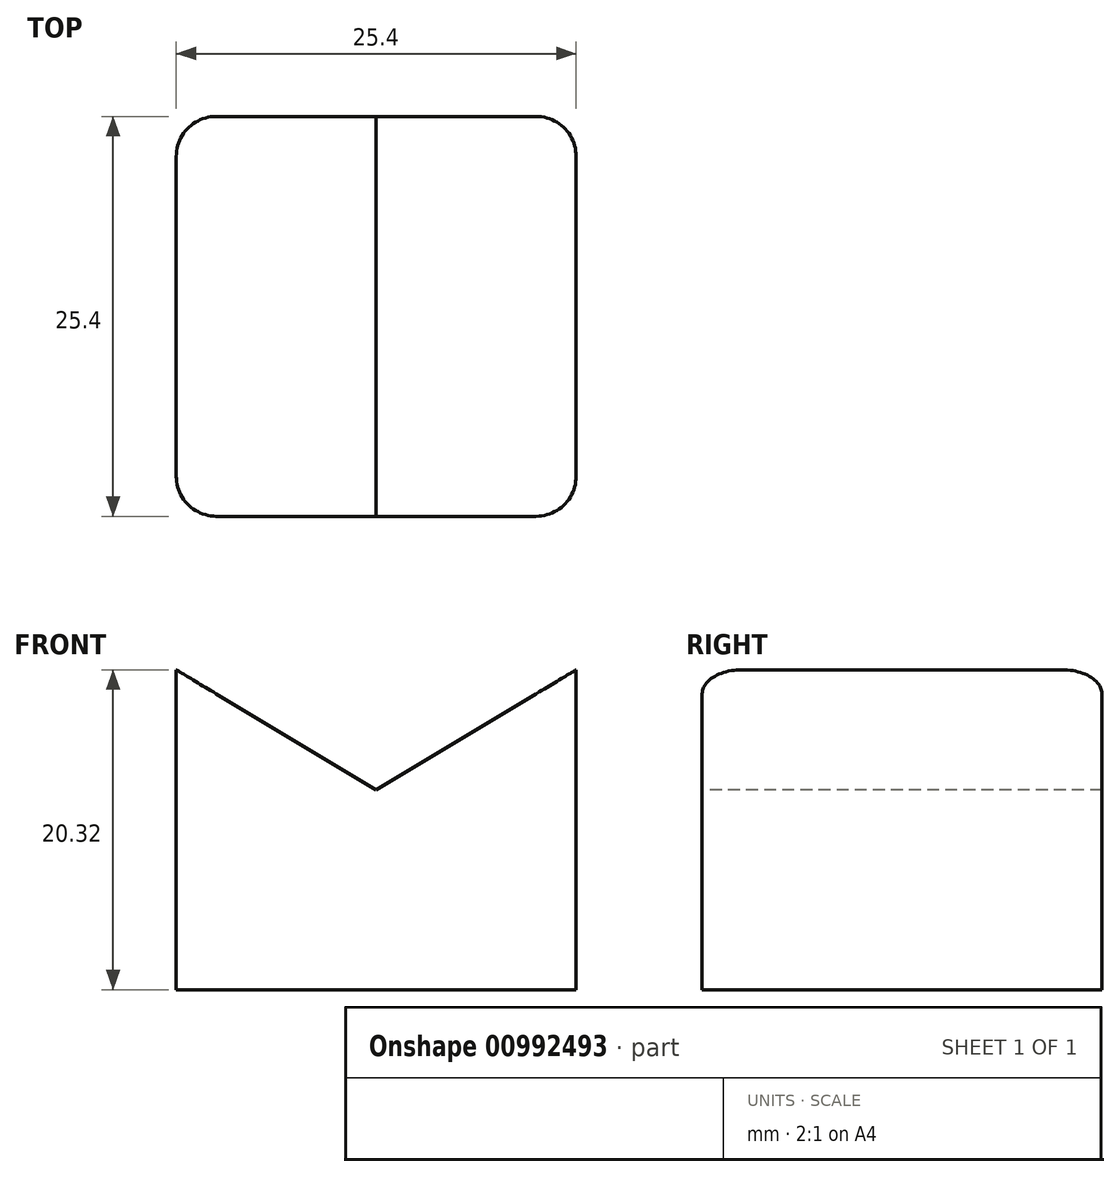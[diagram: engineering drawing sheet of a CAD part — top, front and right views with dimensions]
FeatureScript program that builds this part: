
annotation { "Feature Type Name" : "Feature", "Feature Type Description" : "" }
export const myFeature = defineFeature(function(context is Context, id is Id, definition is map)
    precondition{}
    {
        {
            var Q0;
            Q0=qCreatedBy(makeId("Top.planeOp"),FACE);
            var sketch = newSketch(context, id + "F0", { "sketchPlane" : qUnion([Q0])});
            skLineSegment(sketch, "E0.bottom", {"start": v(2.54, 0) * mm, "end": v(22.86, 0) * mm});
            skLineSegment(sketch, "E0.top", {"start": v(2.54, -25.4) * mm, "end": v(22.86, -25.4) * mm});
            skLineSegment(sketch, "E0.left", {"start": v(0, -2.54) * mm, "end": v(0, -22.86) * mm});
            skLineSegment(sketch, "E0.right", {"start": v(25.4, -2.54) * mm, "end": v(25.4, -22.86) * mm});
            skPoint(sketch, "E1.visualSharp", {"position": v(25.4, 0) * mm});
            skArc(sketch, "E1.filletArc", {"start": v(25.4, -2.54) * mm, "mid": v(24.66, -0.74) * mm, "end": v(22.86, 0) * mm});
            skPoint(sketch, "E2.visualSharp", {"position": v(25.4, -25.4) * mm});
            skArc(sketch, "E2.filletArc", {"start": v(22.86, -25.4) * mm, "mid": v(24.66, -24.66) * mm, "end": v(25.4, -22.86) * mm});
            skPoint(sketch, "E3.visualSharp", {"position": v(0, -25.4) * mm});
            skArc(sketch, "E3.filletArc", {"start": v(0, -22.86) * mm, "mid": v(0.74, -24.66) * mm, "end": v(2.54, -25.4) * mm});
            skPoint(sketch, "E4.visualSharp", {"position": v(0, 0) * mm});
            skArc(sketch, "E4.filletArc", {"start": v(2.54, 0) * mm, "mid": v(0.74, -0.74) * mm, "end": v(0, -2.54) * mm});
            skSolve(sketch);
        }
        {
            var Q0;
            Q0=makeQuery(id+"F0.imprint","IMPRINT",FACE,{"disambiguationData":[TD([[makeQuery(id+"F0.imprint","IMPRINT",EDGE,{"derivedFrom":sQuery(id+"F0.wireOp",EDGE,"E0.bottom")}),-1.0]])]});
            extrude(context, id + "F1", {"entities" : qUnion([Q0]), "depth" : 20.32 * mm, "offsetDistance" : 25.4 * mm});
        }
        {
            var Q0;
            Q0=makeQuery(id+"F1.opExtrude","SWEPT_FACE",FACE,{"disambiguationData":[OSD([sQuery(id+"F0.wireOp",EDGE,"E0.top")])]});
            var sketch = newSketch(context, id + "F2", { "sketchPlane" : qUnion([Q0])});
            skLineSegment(sketch, "E5", {"start": v(12.7, 12.7) * mm, "end": v(0, 20.32) * mm});
            skPoint(sketch, "E5.startSnap0", {"position": v(12.7, 0) * mm});
            skLineSegment(sketch, "E6.0", {"start": v(25.4, 20.32) * mm, "end": v(25.4, 0) * mm});
            skLineSegment(sketch, "E7", {"start": v(12.7, 12.7) * mm, "end": v(25.4, 20.32) * mm});
            skLineSegment(sketch, "E8", {"start": v(0, 20.32) * mm, "end": v(25.4, 20.32) * mm});
            skSolve(sketch);
        }
        {
            var Q0;
            {var subQ0=sQuery(id+"F2.wireOp",EDGE,"E8");var subQ1=sQuery(id+"F2.wireOp",EDGE,"E5");var subQ2=makeQuery(id+"F2.imprint","INTERSECT",VERTEX,{"derivedFrom":[subQ1,subQ0]});Q0=makeQuery(id+"F2.imprint","IMPRINT",FACE,{"disambiguationData":[TD([[makeQuery(id+"F2.imprint","IMPRINT",EDGE,{"disambiguationData":[TD([[subQ2,1.0]])],"derivedFrom":subQ1}),-1.0]])]});}
            var sketch = newSketch(context, id + "F3", { "sketchPlane" : qUnion([Q0])});
            skSolve(sketch);
        }
        {
            var Q0;
            {var subQ4=sQuery(id+"F2.wireOp",EDGE,"E5");var subQ6=sQuery(id+"F2.wireOp",EDGE,"E7");var subQ7=makeQuery(id+"F2.imprint","INTERSECT",VERTEX,{"derivedFrom":[subQ4,subQ6]});Q0=makeQuery(id+"F2.imprint","IMPRINT",FACE,{"disambiguationData":[TD([[makeQuery(id+"F2.imprint","IMPRINT",EDGE,{"disambiguationData":[TD([[subQ7,-1.0]])],"derivedFrom":subQ4}),-1.0]])]});}
            var Q1;
            {var subQ0=sQuery(id+"F2.wireOp",EDGE,"E8");var subQ1=sQuery(id+"F2.wireOp",EDGE,"E7");var subQ2=makeQuery(id+"F2.imprint","INTERSECT",VERTEX,{"derivedFrom":[subQ1,subQ0]});Q1=makeQuery(id+"F2.imprint","IMPRINT",FACE,{"disambiguationData":[TD([[makeQuery(id+"F2.imprint","IMPRINT",EDGE,{"disambiguationData":[TD([[subQ2,1.0]])],"derivedFrom":subQ1}),1.0]])]});}
            var Q2;
            {var subQ0=sQuery(id+"F2.wireOp",EDGE,"E8");var subQ1=sQuery(id+"F2.wireOp",EDGE,"E5");var subQ2=makeQuery(id+"F2.imprint","INTERSECT",VERTEX,{"derivedFrom":[subQ1,subQ0]});Q2=makeQuery(id+"F3.imprint","IMPRINT",FACE,{"disambiguationData":[TD([[makeQuery(id+"F3.imprint","IMPRINT",EDGE,{"derivedFrom":makeQuery(id+"F2.imprint","IMPRINT",EDGE,{"disambiguationData":[TD([[subQ2,1.0]])],"derivedFrom":subQ1})}),-1.0]])]});}
            extrude(context, id + "F4", {"entities" : qUnion([Q0, Q1, Q2]), "operationType" : NewBodyOperationType.REMOVE, "oppositeDirection" : true, "depth" : 25.4 * mm, "offsetDistance" : 25.4 * mm});
        }
    });
